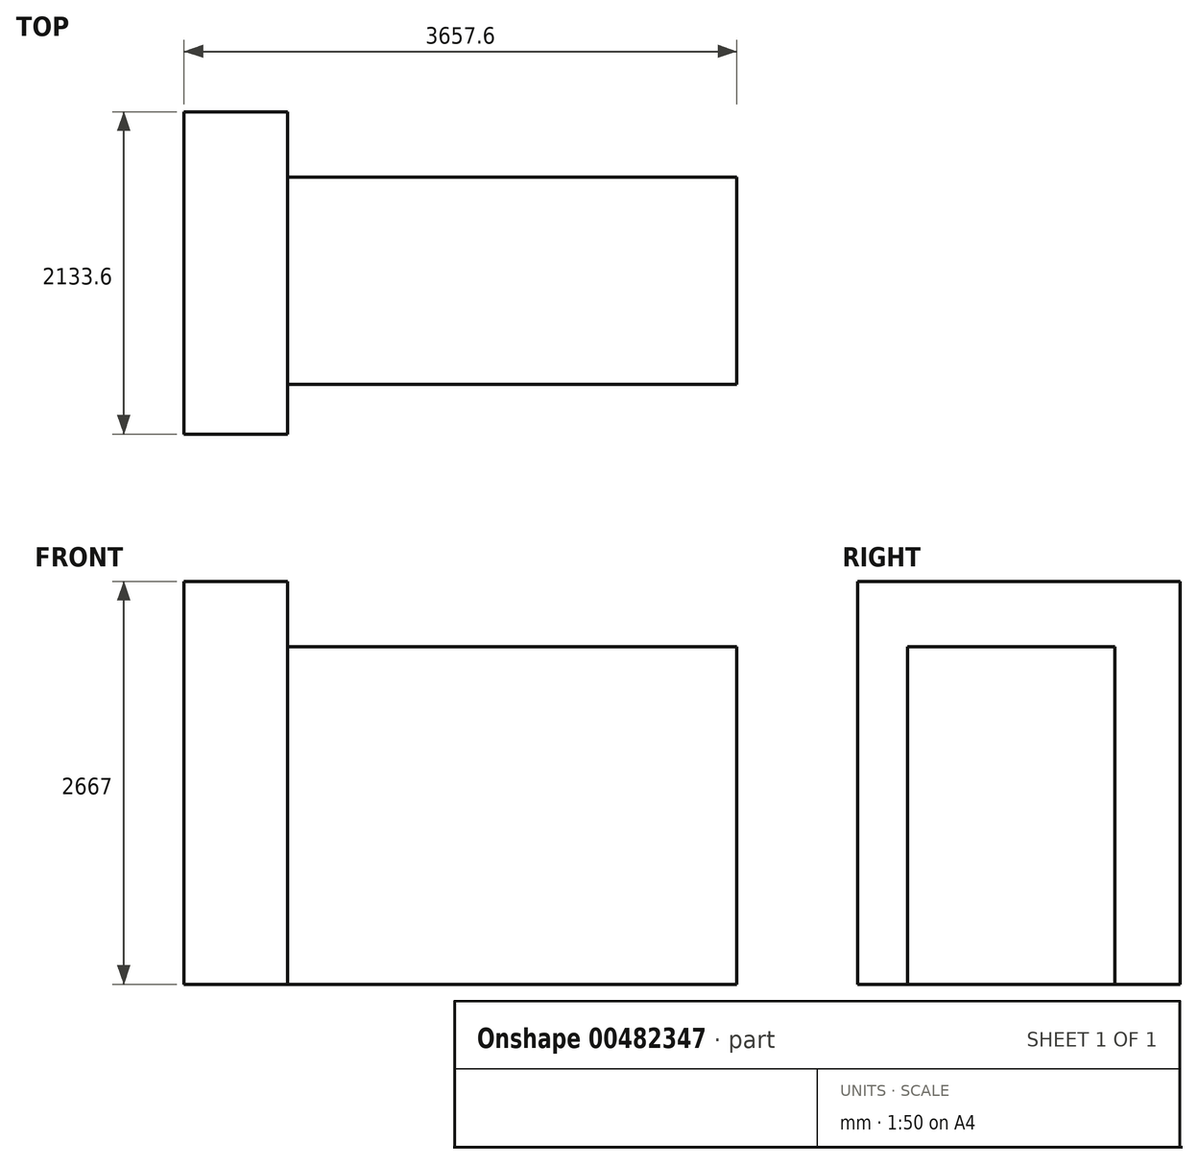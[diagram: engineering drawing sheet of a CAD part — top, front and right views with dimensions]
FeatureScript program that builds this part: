
annotation { "Feature Type Name" : "Feature", "Feature Type Description" : "" }
export const myFeature = defineFeature(function(context is Context, id is Id, definition is map)
    precondition{}
    {
        {
            var Q0;
            Q0=qCreatedBy(makeId("Top.planeOp"),FACE);
            var sketch = newSketch(context, id + "F0", { "sketchPlane" : qUnion([Q0])});
            skLineSegment(sketch, "E0", {"start": v(0, 1066.8) * mm, "end": v(0, -1066.8) * mm});
            skLineSegment(sketch, "E1", {"start": v(0, -1066.8) * mm, "end": v(685.8, -1066.8) * mm});
            skLineSegment(sketch, "E2", {"start": v(685.8, -1066.8) * mm, "end": v(685.8, -736.6) * mm});
            skLineSegment(sketch, "E3", {"start": v(685.8, -736.6) * mm, "end": v(3657.6, -736.6) * mm});
            skLineSegment(sketch, "E4", {"start": v(3657.6, -736.6) * mm, "end": v(3657.6, 635) * mm});
            skLineSegment(sketch, "E5", {"start": v(3657.6, 635) * mm, "end": v(685.8, 635) * mm});
            skLineSegment(sketch, "E6", {"start": v(685.8, 635) * mm, "end": v(685.8, 1066.8) * mm});
            skLineSegment(sketch, "E7", {"start": v(685.8, 1066.8) * mm, "end": v(0, 1066.8) * mm});
            skSolve(sketch);
        }
        {
            var Q0;
            Q0 = qSketchRegion(id + "F0", true);
            extrude(context, id + "F1", {"entities" : qUnion([Q0]), "depth" : 2667 * mm, "offsetDistance" : 25.4 * mm});
        }
        {
            var Q0;
            Q0=makeQuery(id+"F1.opExtrude","SWEPT_FACE",FACE,{"disambiguationData":[OSD([sQuery(id+"F0.wireOp",EDGE,"E3")])]});
            var sketch = newSketch(context, id + "F2", { "sketchPlane" : qUnion([Q0])});
            skLineSegment(sketch, "E8.bottom", {"start": v(685.8, 2667) * mm, "end": v(3657.6, 2667) * mm});
            skLineSegment(sketch, "E8.top", {"start": v(685.8, 2235.2) * mm, "end": v(3657.6, 2235.2) * mm});
            skLineSegment(sketch, "E8.left", {"start": v(685.8, 2667) * mm, "end": v(685.8, 2235.2) * mm});
            skLineSegment(sketch, "E8.right", {"start": v(3657.6, 2667) * mm, "end": v(3657.6, 2235.2) * mm});
            skSolve(sketch);
        }
        {
            var Q0;
            Q0 = qSketchRegion(id + "F2", true);
            extrude(context, id + "F3", {"entities" : qUnion([Q0]), "operationType" : NewBodyOperationType.REMOVE, "endBound" : BoundingType.THROUGH_ALL, "oppositeDirection" : true, "depth" : 25.4 * mm, "offsetDistance" : 25.4 * mm});
        }
    });
